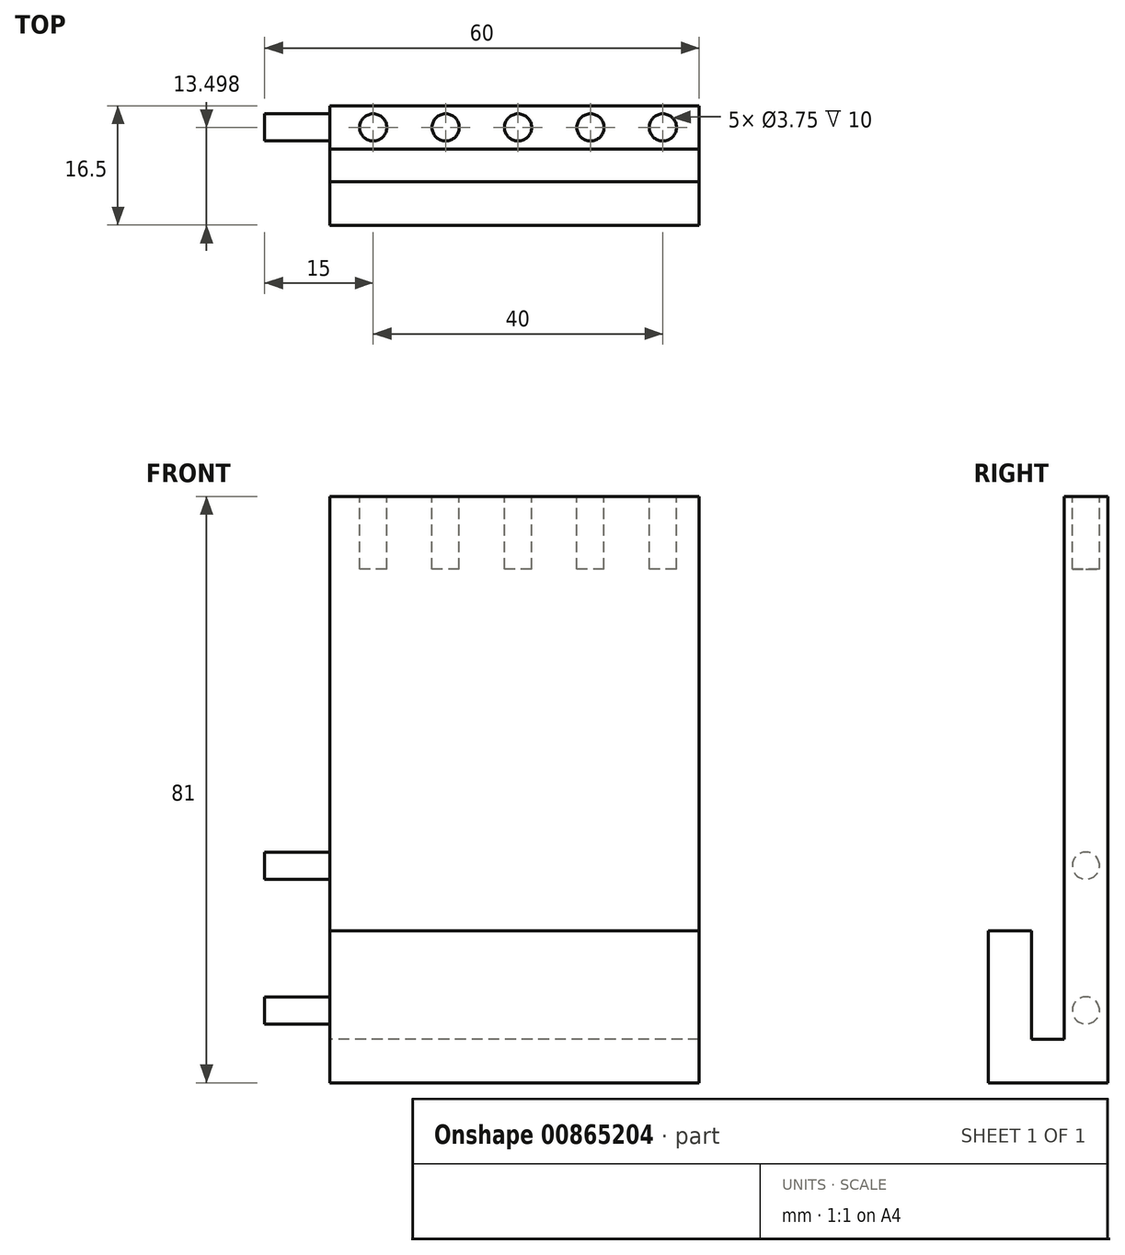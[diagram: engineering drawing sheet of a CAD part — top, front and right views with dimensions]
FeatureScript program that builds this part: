
annotation { "Feature Type Name" : "Feature", "Feature Type Description" : "" }
export const myFeature = defineFeature(function(context is Context, id is Id, definition is map)
    precondition{}
    {
        {
            var Q0;
            Q0=qCreatedBy(makeId("Right.planeOp"),FACE);
            var sketch = newSketch(context, id + "F0", { "sketchPlane" : qUnion([Q0])});
            skLineSegment(sketch, "E0", {"start": v(-0.52, -27.12) * mm, "end": v(15.98, -27.12) * mm});
            skLineSegment(sketch, "E1", {"start": v(-0.52, -27.12) * mm, "end": v(-0.52, -6.12) * mm});
            skLineSegment(sketch, "E2", {"start": v(5.48, -6.12) * mm, "end": v(5.48, -21.12) * mm});
            skLineSegment(sketch, "E3", {"start": v(5.48, -21.12) * mm, "end": v(9.98, -21.12) * mm});
            skLineSegment(sketch, "E4", {"start": v(9.98, -21.12) * mm, "end": v(9.98, 53.88) * mm});
            skLineSegment(sketch, "E5", {"start": v(-0.52, -6.12) * mm, "end": v(5.48, -6.12) * mm});
            skLineSegment(sketch, "E6", {"start": v(15.98, -27.12) * mm, "end": v(15.98, 53.88) * mm});
            skLineSegment(sketch, "E7", {"start": v(15.98, 53.88) * mm, "end": v(9.98, 53.88) * mm});
            skSolve(sketch);
        }
        {
            var Q0;
            Q0=makeQuery(id+"F0.imprint","IMPRINT",FACE,{"disambiguationData":[TD([[makeQuery(id+"F0.imprint","IMPRINT",EDGE,{"derivedFrom":sQuery(id+"F0.wireOp",EDGE,"E0")}),1.0]])]});
            extrude(context, id + "F1", {"entities" : qUnion([Q0]), "depth" : 60 * mm, "offsetDistance" : 25 * mm});
        }
        {
            var Q0;
            Q0=makeQuery(id+"F1.opExtrude","CAP_FACE",FACE,{"disambiguationData":[OSD([sQuery(id+"F0.wireOp",EDGE,"2XUTt1vI-pfQM-6Z4u-z1Qd-fw7XdaFohFqD"),sQuery(id+"F0.wireOp",EDGE,"E0"),sQuery(id+"F0.wireOp",EDGE,"E1"),sQuery(id+"F0.wireOp",EDGE,"E2"),sQuery(id+"F0.wireOp",EDGE,"E3"),sQuery(id+"F0.wireOp",EDGE,"E4"),sQuery(id+"F0.wireOp",EDGE,"m4hJhome-FK86-Fo4P-3xqC-MsUvg3DtBtmv"),sQuery(id+"F0.wireOp",EDGE,"E5")])],"isStart":true});
            var sketch = newSketch(context, id + "F2", { "sketchPlane" : qUnion([Q0])});
            skCircle(sketch, "E8", {"center": v(-12.98, 43.88) * mm, "radius": 1.88 * mm});
            skCircle(sketch, "E9", {"center": v(-12.98, 23.88) * mm, "radius": 1.88 * mm});
            skCircle(sketch, "E10.MirrorC", {"center": v(-12.98, -17.12) * mm, "radius": 1.88 * mm});
            skCircle(sketch, "E11.MirrorC", {"center": v(-12.98, 2.88) * mm, "radius": 1.88 * mm});
            skLineSegment(sketch, "E12", {"start": v(-12.98, 53.88) * mm, "end": v(-12.98, 43.88) * mm});
            skLineSegment(sketch, "E13", {"start": v(-12.98, 43.88) * mm, "end": v(-12.98, 23.88) * mm});
            skLineSegment(sketch, "E14", {"start": v(-12.98, 23.88) * mm, "end": v(-12.98, 2.88) * mm});
            skLineSegment(sketch, "E15", {"start": v(-12.98, 2.88) * mm, "end": v(-12.98, -17.12) * mm});
            skLineSegment(sketch, "E16", {"start": v(-12.98, -17.12) * mm, "end": v(-12.98, -27.12) * mm});
            skSolve(sketch);
        }
        {
            var Q0;
            {var subQ0=sQuery(id+"F2.wireOp",EDGE,"E12");var subQ1=sQuery(id+"F2.wireOp",EDGE,"E8");var subQ2=makeQuery(id+"F2.imprint","INTERSECT",VERTEX,{"derivedFrom":[subQ1,subQ0]});Q0=makeQuery(id+"F2.imprint","IMPRINT",FACE,{"disambiguationData":[TD([[makeQuery(id+"F2.imprint","IMPRINT",EDGE,{"disambiguationData":[TD([[subQ2,1.0]])],"derivedFrom":subQ1}),1.0]])]});}
            var Q1;
            {var subQ0=sQuery(id+"F2.wireOp",EDGE,"E12");var subQ1=sQuery(id+"F2.wireOp",EDGE,"E8");var subQ2=makeQuery(id+"F2.imprint","INTERSECT",VERTEX,{"derivedFrom":[subQ1,subQ0]});Q1=makeQuery(id+"F2.imprint","IMPRINT",FACE,{"disambiguationData":[TD([[makeQuery(id+"F2.imprint","IMPRINT",EDGE,{"disambiguationData":[TD([[subQ2,-1.0]])],"derivedFrom":subQ1}),1.0]])]});}
            var Q2;
            {var subQ0=sQuery(id+"F2.wireOp",EDGE,"E13");var subQ1=sQuery(id+"F2.wireOp",EDGE,"E9");var subQ2=makeQuery(id+"F2.imprint","INTERSECT",VERTEX,{"derivedFrom":[subQ1,subQ0]});Q2=makeQuery(id+"F2.imprint","IMPRINT",FACE,{"disambiguationData":[TD([[makeQuery(id+"F2.imprint","IMPRINT",EDGE,{"disambiguationData":[TD([[subQ2,1.0]])],"derivedFrom":subQ1}),1.0]])]});}
            var Q3;
            {var subQ0=sQuery(id+"F2.wireOp",EDGE,"E13");var subQ1=sQuery(id+"F2.wireOp",EDGE,"E9");var subQ2=makeQuery(id+"F2.imprint","INTERSECT",VERTEX,{"derivedFrom":[subQ1,subQ0]});Q3=makeQuery(id+"F2.imprint","IMPRINT",FACE,{"disambiguationData":[TD([[makeQuery(id+"F2.imprint","IMPRINT",EDGE,{"disambiguationData":[TD([[subQ2,-1.0]])],"derivedFrom":subQ1}),1.0]])]});}
            var Q4;
            {var subQ0=sQuery(id+"F2.wireOp",EDGE,"E14");var subQ1=sQuery(id+"F2.wireOp",EDGE,"E11.MirrorC");var subQ2=makeQuery(id+"F2.imprint","INTERSECT",VERTEX,{"derivedFrom":[subQ1,subQ0]});Q4=makeQuery(id+"F2.imprint","IMPRINT",FACE,{"disambiguationData":[TD([[makeQuery(id+"F2.imprint","IMPRINT",EDGE,{"disambiguationData":[TD([[subQ2,-1.0]])],"derivedFrom":subQ1}),-1.0]])]});}
            var Q5;
            {var subQ0=sQuery(id+"F2.wireOp",EDGE,"E14");var subQ1=sQuery(id+"F2.wireOp",EDGE,"E11.MirrorC");var subQ2=makeQuery(id+"F2.imprint","INTERSECT",VERTEX,{"derivedFrom":[subQ1,subQ0]});Q5=makeQuery(id+"F2.imprint","IMPRINT",FACE,{"disambiguationData":[TD([[makeQuery(id+"F2.imprint","IMPRINT",EDGE,{"disambiguationData":[TD([[subQ2,1.0]])],"derivedFrom":subQ1}),-1.0]])]});}
            var Q6;
            {var subQ0=sQuery(id+"F2.wireOp",EDGE,"E15");var subQ1=sQuery(id+"F2.wireOp",EDGE,"E10.MirrorC");var subQ2=makeQuery(id+"F2.imprint","INTERSECT",VERTEX,{"derivedFrom":[subQ1,subQ0]});Q6=makeQuery(id+"F2.imprint","IMPRINT",FACE,{"disambiguationData":[TD([[makeQuery(id+"F2.imprint","IMPRINT",EDGE,{"disambiguationData":[TD([[subQ2,-1.0]])],"derivedFrom":subQ1}),-1.0]])]});}
            var Q7;
            {var subQ0=sQuery(id+"F2.wireOp",EDGE,"E15");var subQ1=sQuery(id+"F2.wireOp",EDGE,"E10.MirrorC");var subQ2=makeQuery(id+"F2.imprint","INTERSECT",VERTEX,{"derivedFrom":[subQ1,subQ0]});Q7=makeQuery(id+"F2.imprint","IMPRINT",FACE,{"disambiguationData":[TD([[makeQuery(id+"F2.imprint","IMPRINT",EDGE,{"disambiguationData":[TD([[subQ2,1.0]])],"derivedFrom":subQ1}),-1.0]])]});}
            extrude(context, id + "F3", {"entities" : qUnion([Q0, Q1, Q2, Q3, Q4, Q5, Q6, Q7]), "operationType" : NewBodyOperationType.REMOVE, "oppositeDirection" : true, "depth" : 9 * mm, "offsetDistance" : 25 * mm});
        }
        {
            var Q0;
            Q0=makeQuery(id+"F1.opExtrude","SWEPT_FACE",FACE,{"disambiguationData":[OSD([sQuery(id+"F0.wireOp",EDGE,"E7")])]});
            var sketch = newSketch(context, id + "F4", { "sketchPlane" : qUnion([Q0])});
            skLineSegment(sketch, "E17", {"start": v(55, 12.98) * mm, "end": v(45, 12.98) * mm});
            skLineSegment(sketch, "E18", {"start": v(45, 12.98) * mm, "end": v(35, 12.98) * mm});
            skLineSegment(sketch, "E19", {"start": v(35, 12.98) * mm, "end": v(25, 12.98) * mm});
            skLineSegment(sketch, "E20", {"start": v(25, 12.98) * mm, "end": v(15, 12.98) * mm});
            skCircle(sketch, "E21", {"center": v(55, 12.98) * mm, "radius": 1.88 * mm});
            skCircle(sketch, "E22", {"center": v(45, 12.98) * mm, "radius": 1.88 * mm});
            skCircle(sketch, "E23", {"center": v(35, 12.98) * mm, "radius": 1.88 * mm});
            skCircle(sketch, "E24", {"center": v(25, 12.98) * mm, "radius": 1.88 * mm});
            skCircle(sketch, "E25", {"center": v(15, 12.98) * mm, "radius": 1.88 * mm});
            skLineSegment(sketch, "E26", {"start": v(55, 12.98) * mm, "end": v(60, 12.98) * mm});
            skLineSegment(sketch, "E27", {"start": v(60, 12.98) * mm, "end": v(60, 15.98) * mm});
            skSolve(sketch);
        }
        {
            var Q0;
            Q0=qSketchRegion(id+"F4",true);
            extrude(context, id + "F5", {"entities" : qUnion([Q0]), "operationType" : NewBodyOperationType.REMOVE, "oppositeDirection" : true, "depth" : 10 * mm, "offsetDistance" : 25 * mm});
        }
    });
